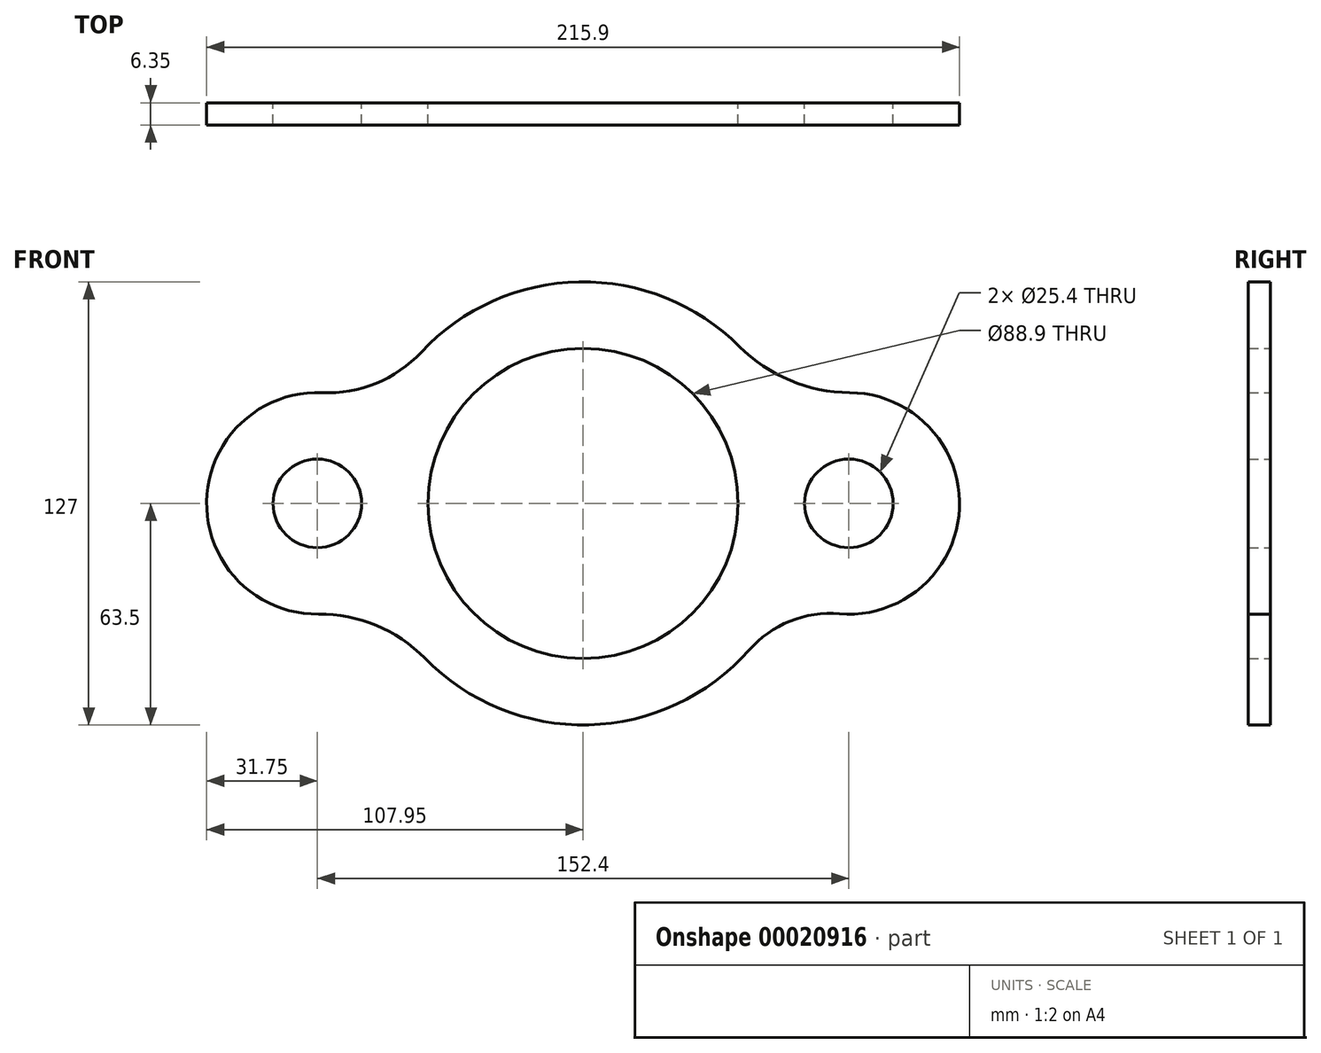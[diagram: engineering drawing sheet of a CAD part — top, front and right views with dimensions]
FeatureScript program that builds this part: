
annotation { "Feature Type Name" : "Feature", "Feature Type Description" : "" }
export const myFeature = defineFeature(function(context is Context, id is Id, definition is map)
    precondition{}
    {
        {
            var Q0;
            Q0=qCreatedBy(makeId("Front.planeOp"),FACE);
            var sketch = newSketch(context, id + "F0", { "sketchPlane" : qUnion([Q0])});
            skCircle(sketch, "E0", {"center": v(0, 0) * mm, "radius": 44.45 * mm});
            skCircle(sketch, "E1", {"center": v(76.2, 0) * mm, "radius": 12.7 * mm});
            skCircle(sketch, "E2", {"center": v(-76.2, 0) * mm, "radius": 12.7 * mm});
            skArc(sketch, "E3", {"start": v(-74.83, 31.72) * mm, "mid": v(-107.95, 0.51) * mm, "end": v(-75.86, -31.75) * mm});
            skArc(sketch, "E4", {"start": v(73.55, -31.64) * mm, "mid": v(107.92, -1.45) * mm, "end": v(76.44, 31.75) * mm});
            skArc(sketch, "E5", {"start": v(-45.42, -44.38) * mm, "mid": v(1.58, -63.48) * mm, "end": v(47.57, -42.07) * mm});
            skArc(sketch, "E6", {"start": v(44.84, 44.96) * mm, "mid": v(59.35, 35.25) * mm, "end": v(76.44, 31.75) * mm});
            skArc(sketch, "E7", {"start": v(73.55, -31.64) * mm, "mid": v(59.33, -33.78) * mm, "end": v(47.57, -42.07) * mm});
            skArc(sketch, "E8", {"start": v(-74.83, 31.72) * mm, "mid": v(-59.35, 34.42) * mm, "end": v(-46.4, 43.35) * mm});
            skArc(sketch, "E9", {"start": v(-45.42, -44.38) * mm, "mid": v(-59.35, -34.95) * mm, "end": v(-75.86, -31.75) * mm});
            skArc(sketch, "E10.trimOffspring", {"start": v(44.84, 44.96) * mm, "mid": v(-1.12, 63.5) * mm, "end": v(-46.4, 43.35) * mm});
            skSolve(sketch);
        }
        {
            var Q0;
            {var subQ0=sQuery(id+"F0.wireOp",EDGE,"ae1b4322-2566-4b04-b388-421c8214b478");var subQ2=sQuery(id+"F0.wireOp",EDGE,"E3");var subQ3=makeQuery(id+"F0.imprint","INTERSECT",VERTEX,{"disambiguationData":[OD(0.0)],"derivedFrom":[subQ2,subQ0]});Q0=makeQuery(id+"F0.imprint","IMPRINT",FACE,{"disambiguationData":[TD([[makeQuery(id+"F0.imprint","IMPRINT",EDGE,{"disambiguationData":[TD([[subQ3,-1.0]])],"derivedFrom":subQ2}),1.0]])]});}
            var Q1;
            {var subQ1=sQuery(id+"F0.wireOp",EDGE,"E2");var subQ5=sQuery(id+"F0.wireOp",EDGE,"E5");var subQ7=makeQuery(id+"F0.imprint","INTERSECT",VERTEX,{"derivedFrom":[subQ1,subQ5]});Q1=makeQuery(id+"F0.imprint","IMPRINT",FACE,{"disambiguationData":[TD([[makeQuery(id+"F0.imprint","IMPRINT",EDGE,{"disambiguationData":[TD([[subQ7,1.0]])],"derivedFrom":subQ1}),-1.0]])]});}
            var Q2;
            {var subQ1=sQuery(id+"F0.wireOp",EDGE,"E3");var subQ5=makeQuery(id+"F0.imprint","INTERSECT",VERTEX,{"derivedFrom":[sQuery(id+"F0.wireOp",EDGE,"E0"),subQ1]});Q2=makeQuery(id+"F0.imprint","IMPRINT",FACE,{"disambiguationData":[TD([[makeQuery(id+"F0.imprint","IMPRINT",EDGE,{"disambiguationData":[TD([[subQ5,-1.0]])],"derivedFrom":subQ1}),1.0]])]});}
            var Q3;
            {var subQ1=sQuery(id+"F0.wireOp",EDGE,"E2");var subQ5=sQuery(id+"F0.wireOp",EDGE,"E5");var subQ7=makeQuery(id+"F0.imprint","INTERSECT",VERTEX,{"derivedFrom":[subQ1,subQ5]});Q3=makeQuery(id+"F0.imprint","IMPRINT",FACE,{"disambiguationData":[TD([[makeQuery(id+"F0.imprint","IMPRINT",EDGE,{"disambiguationData":[TD([[subQ7,-1.0]])],"derivedFrom":subQ1}),-1.0]])]});}
            var Q4;
            {var subQ0=sQuery(id+"F0.wireOp",EDGE,"E8");Q4=makeQuery(id+"F0.imprint","IMPRINT",FACE,{"disambiguationData":[TD([[makeQuery(id+"F0.imprint","IMPRINT",EDGE,{"derivedFrom":subQ0}),-1.0]])]});}
            var Q5;
            {var subQ5=sQuery(id+"F0.wireOp",EDGE,"E3");var subQ7=sQuery(id+"F0.wireOp",EDGE,"E0");var subQ9=makeQuery(id+"F0.imprint","INTERSECT",VERTEX,{"derivedFrom":[subQ7,subQ5]});Q5=makeQuery(id+"F0.imprint","IMPRINT",FACE,{"disambiguationData":[TD([[makeQuery(id+"F0.imprint","IMPRINT",EDGE,{"disambiguationData":[TD([[subQ9,1.0]])],"derivedFrom":subQ7}),-1.0]])]});}
            var Q6;
            {var subQ1=sQuery(id+"F0.wireOp",EDGE,"E4");var subQ5=makeQuery(id+"F0.imprint","INTERSECT",VERTEX,{"derivedFrom":[sQuery(id+"F0.wireOp",EDGE,"E0"),subQ1]});Q6=makeQuery(id+"F0.imprint","IMPRINT",FACE,{"disambiguationData":[TD([[makeQuery(id+"F0.imprint","IMPRINT",EDGE,{"disambiguationData":[TD([[subQ5,1.0]])],"derivedFrom":subQ1}),1.0]])]});}
            var Q7;
            {var subQ0=sQuery(id+"F0.wireOp",EDGE,"E7");Q7=makeQuery(id+"F0.imprint","IMPRINT",FACE,{"disambiguationData":[TD([[makeQuery(id+"F0.imprint","IMPRINT",EDGE,{"derivedFrom":subQ0}),-1.0]])]});}
            var Q8;
            {var subQ3=sQuery(id+"F0.wireOp",EDGE,"E1");Q8=makeQuery(id+"F0.imprint","IMPRINT",FACE,{"disambiguationData":[TD([[makeQuery(id+"F0.imprint","IMPRINT",EDGE,{"derivedFrom":subQ3}),-1.0]])]});}
            var Q9;
            {var subQ0=sQuery(id+"F0.wireOp",EDGE,"E6");Q9=makeQuery(id+"F0.imprint","IMPRINT",FACE,{"disambiguationData":[TD([[makeQuery(id+"F0.imprint","IMPRINT",EDGE,{"derivedFrom":subQ0}),-1.0]])]});}
            var Q10;
            {var subQ5=sQuery(id+"F0.wireOp",EDGE,"E3");var subQ7=sQuery(id+"F0.wireOp",EDGE,"E0");var subQ9=makeQuery(id+"F0.imprint","INTERSECT",VERTEX,{"derivedFrom":[subQ7,subQ5]});Q10=makeQuery(id+"F0.imprint","IMPRINT",FACE,{"disambiguationData":[TD([[makeQuery(id+"F0.imprint","IMPRINT",EDGE,{"disambiguationData":[TD([[subQ9,-1.0]])],"derivedFrom":subQ7}),-1.0]])]});}
            extrude(context, id + "F1", {"entities" : qUnion([Q0, Q1, Q2, Q3, Q4, Q5, Q6, Q7, Q8, Q9, Q10]), "depth" : 6.35 * mm});
        }
    });
